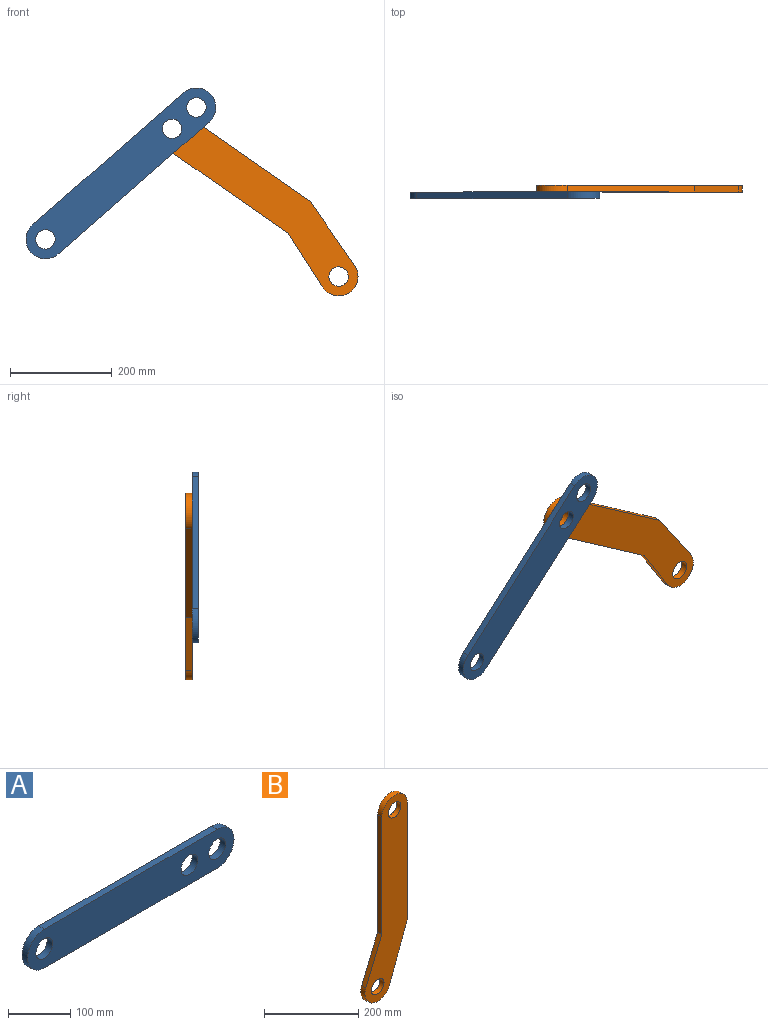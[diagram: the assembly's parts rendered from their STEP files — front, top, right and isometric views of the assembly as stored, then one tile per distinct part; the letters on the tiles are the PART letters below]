
ASSEMBLY  parts=2 mates=1
PART A: 9 faces, bbox 469.9x12.7x76.2 mm
  f0: cylinder r=38.1mm len=76.2mm, axis (0,1,0), area 1520.1mm2, adj f1,f4,f7,f8
  f1: plane 393.7x12.7mm, normal (0,0,-1), area 5000mm2, adj f0,f2,f7,f8
  f2: cylinder r=38.1mm len=76.2mm, axis (0,1,0), area 1520.1mm2, adj f1,f4,f7,f8
  f3: cylinder r=19.05mm len=38.1mm, axis (0,1,0), area 1520.1mm2, adj f7,f8
  f4: plane 393.7x12.7mm, normal (0,0,1), area 5000mm2, adj f0,f2,f7,f8
  f5: cylinder r=19.05mm len=38.1mm, axis (0,1,0), area 1520.1mm2, adj f7,f8
  f6: cylinder r=19.05mm len=38.1mm, axis (0,1,0), area 1520.1mm2, adj f7,f8
  f7: plane 469.9x76.2mm, normal (0,-1,0), area 31140mm2, adj f0,f1,f2,f3,f4,f5,f6
  f8: plane 469.9x76.2mm, normal (0,1,0), area 31140mm2, adj f0,f1,f2,f3,f4,f5,f6
PART B: 10 faces, bbox 126.9x12.7x510.6 mm
  f0: cylinder r=38.1mm len=76.2mm, axis (0,1,0), area 1520.1mm2, adj f1,f5,f8,f9
  f1: plane 304.8x12.7mm, normal (-1,0,0), area 3871mm2, adj f0,f2,f8,f9
  f2: plane 114.93x47.81mm, normal (-0.92,0,0.38), area 1580.9mm2, adj f1,f3,f8,f9
  f3: cylinder r=38.1mm len=73.81mm, axis (0,1,0), area 1538.6mm2, adj f2,f4,f8,f9
  f4: plane 142.84x53.12mm, normal (0.94,0,-0.35), area 1935.5mm2, adj f3,f5,f8,f9
  f5: plane 304.8x12.7mm, normal (1,0,0), area 3871mm2, adj f0,f4,f8,f9
  f6: cylinder r=19.05mm len=38.1mm, axis (0,1,0), area 1520.1mm2, adj f8,f9
  f7: cylinder r=19.05mm len=38.1mm, axis (0,1,0), area 1520.1mm2, adj f8,f9
  f8: plane 510.56x126.93mm, normal (0,-1,0), area 35744.5mm2, adj f0,f1,f2,f3,f4,f5,f6,f7
  f9: plane 510.56x126.93mm, normal (0,1,0), area 35744.5mm2, adj f0,f1,f2,f3,f4,f5,f6,f7
PLACE A rot(axis=(0,-1,0),41.1deg) t=(-144.78,17.32,363.72)mm
PLACE B rot(axis=(0,-1,0),55.1deg) t=(103.88,30.02,580.98)mm
MATE revolute B.f6 <-> A.f3  axis (0,-1,0) through (103.88,17.32,580.98)mm
